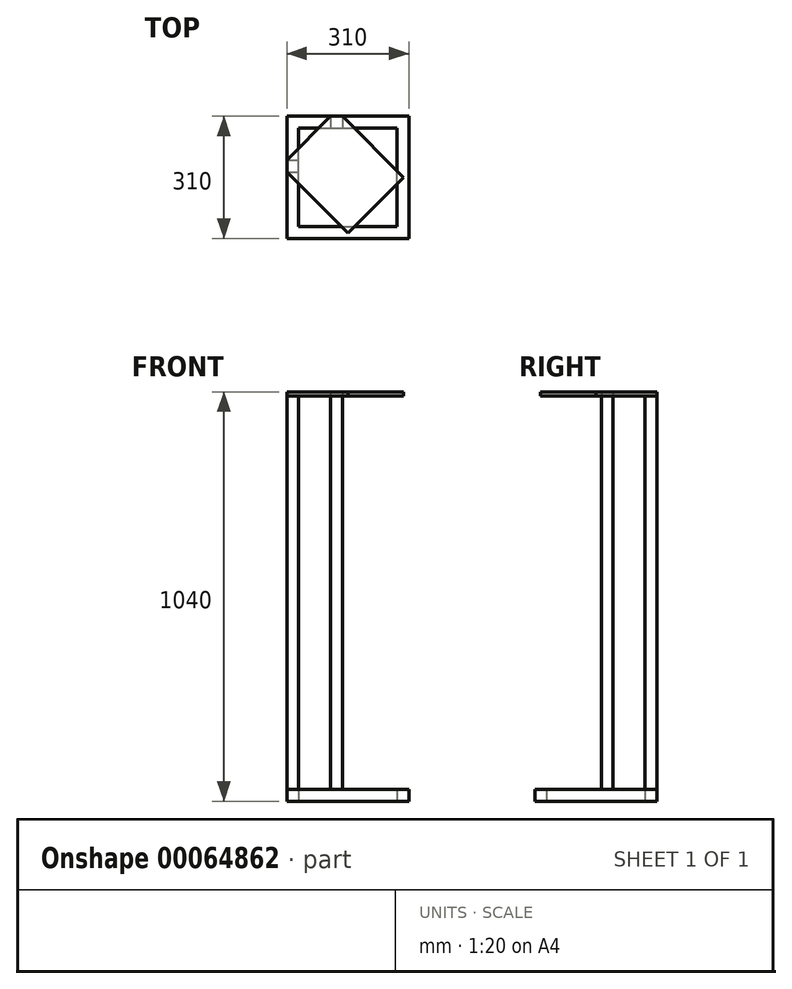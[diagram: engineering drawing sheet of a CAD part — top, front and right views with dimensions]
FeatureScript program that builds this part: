
annotation { "Feature Type Name" : "Feature", "Feature Type Description" : "" }
export const myFeature = defineFeature(function(context is Context, id is Id, definition is map)
    precondition{}
    {
        {
            var Q0;
            Q0=qCreatedBy(makeId("Top.planeOp"),FACE);
            var sketch = newSketch(context, id + "F0", { "sketchPlane" : qUnion([Q0])});
            skLineSegment(sketch, "E0.rect.bottom", {"start": v(-125, -125) * mm, "end": v(125, -125) * mm});
            skLineSegment(sketch, "E0.rect.top", {"start": v(-125, 125) * mm, "end": v(125, 125) * mm});
            skLineSegment(sketch, "E0.rect.left", {"start": v(-125, -125) * mm, "end": v(-125, 125) * mm});
            skLineSegment(sketch, "E0.rect.right", {"start": v(125, -125) * mm, "end": v(125, 125) * mm});
            skPoint(sketch, "E0.rect.middle", {"position": v(0, 0) * mm});
            skLineSegment(sketch, "E1.0", {"start": v(155, -155) * mm, "end": v(155, 155) * mm});
            skLineSegment(sketch, "E1.1", {"start": v(-155, -155) * mm, "end": v(155, -155) * mm});
            skLineSegment(sketch, "E1.2", {"start": v(-155, -155) * mm, "end": v(-155, 155) * mm});
            skLineSegment(sketch, "E1.3", {"start": v(-155, 155) * mm, "end": v(155, 155) * mm});
            skSolve(sketch);
        }
        {
            var Q0;
            Q0 = qSketchRegion(id + "F0", true);
            extrude(context, id + "F1", {"entities" : qUnion([Q0]), "depth" : 30 * mm});
        }
        {
            var Q0;
            Q0=makeQuery(id+"F1.opExtrude","CAP_FACE",FACE,{"disambiguationData":[OSD([sQuery(id+"F0.wireOp",EDGE,"E0.rect.bottom"),sQuery(id+"F0.wireOp",EDGE,"E0.rect.top"),sQuery(id+"F0.wireOp",EDGE,"E0.rect.left"),sQuery(id+"F0.wireOp",EDGE,"E0.rect.right"),sQuery(id+"F0.wireOp",EDGE,"E1.0"),sQuery(id+"F0.wireOp",EDGE,"E1.1"),sQuery(id+"F0.wireOp",EDGE,"E1.2"),sQuery(id+"F0.wireOp",EDGE,"E1.3")])],"isStart":false});
            var sketch = newSketch(context, id + "F2", { "sketchPlane" : qUnion([Q0])});
            skLineSegment(sketch, "E2.bottom", {"start": v(-44, 155) * mm, "end": v(-14, 155) * mm});
            skLineSegment(sketch, "E2.top", {"start": v(-44, 125) * mm, "end": v(-14, 125) * mm});
            skLineSegment(sketch, "E2.left", {"start": v(-44, 155) * mm, "end": v(-44, 125) * mm});
            skLineSegment(sketch, "E2.right", {"start": v(-14, 155) * mm, "end": v(-14, 125) * mm});
            skLineSegment(sketch, "E3.bottom", {"start": v(-155, 44) * mm, "end": v(-125, 44) * mm});
            skLineSegment(sketch, "E3.top", {"start": v(-155, 14) * mm, "end": v(-125, 14) * mm});
            skLineSegment(sketch, "E3.left", {"start": v(-155, 44) * mm, "end": v(-155, 14) * mm});
            skLineSegment(sketch, "E3.right", {"start": v(-125, 44) * mm, "end": v(-125, 14) * mm});
            skSolve(sketch);
        }
        {
            var Q0;
            Q0 = qSketchRegion(id + "F2", true);
            extrude(context, id + "F3", {"entities" : qUnion([Q0]), "operationType" : NewBodyOperationType.ADD, "depth" : 1000 * mm});
        }
        {
            var Q0;
            Q0=makeQuery(id+"F3.opExtrude","CAP_FACE",FACE,{"disambiguationData":[OSD([sQuery(id+"F2.wireOp",EDGE,"E3.bottom"),sQuery(id+"F2.wireOp",EDGE,"E3.top"),sQuery(id+"F2.wireOp",EDGE,"E3.left"),sQuery(id+"F2.wireOp",EDGE,"E3.right")])],"isStart":false});
            var sketch = newSketch(context, id + "F4", { "sketchPlane" : qUnion([Q0])});
            skLineSegment(sketch, "E4", {"start": v(-155, 44) * mm, "end": v(-44, 155) * mm});
            skLineSegment(sketch, "E5", {"start": v(-155, 44) * mm, "end": v(-155, 14) * mm});
            skLineSegment(sketch, "E6", {"start": v(-155, 14) * mm, "end": v(0, -141) * mm});
            skLineSegment(sketch, "E7", {"start": v(0, -141) * mm, "end": v(141, 0) * mm});
            skLineSegment(sketch, "E8", {"start": v(141, 0) * mm, "end": v(-14, 155) * mm});
            skLineSegment(sketch, "E9", {"start": v(-14, 155) * mm, "end": v(-44, 155) * mm});
            skSolve(sketch);
        }
        {
            var Q0;
            Q0 = qSketchRegion(id + "F4", true);
            extrude(context, id + "F5", {"entities" : qUnion([Q0]), "depth" : 10 * mm});
        }
    });
